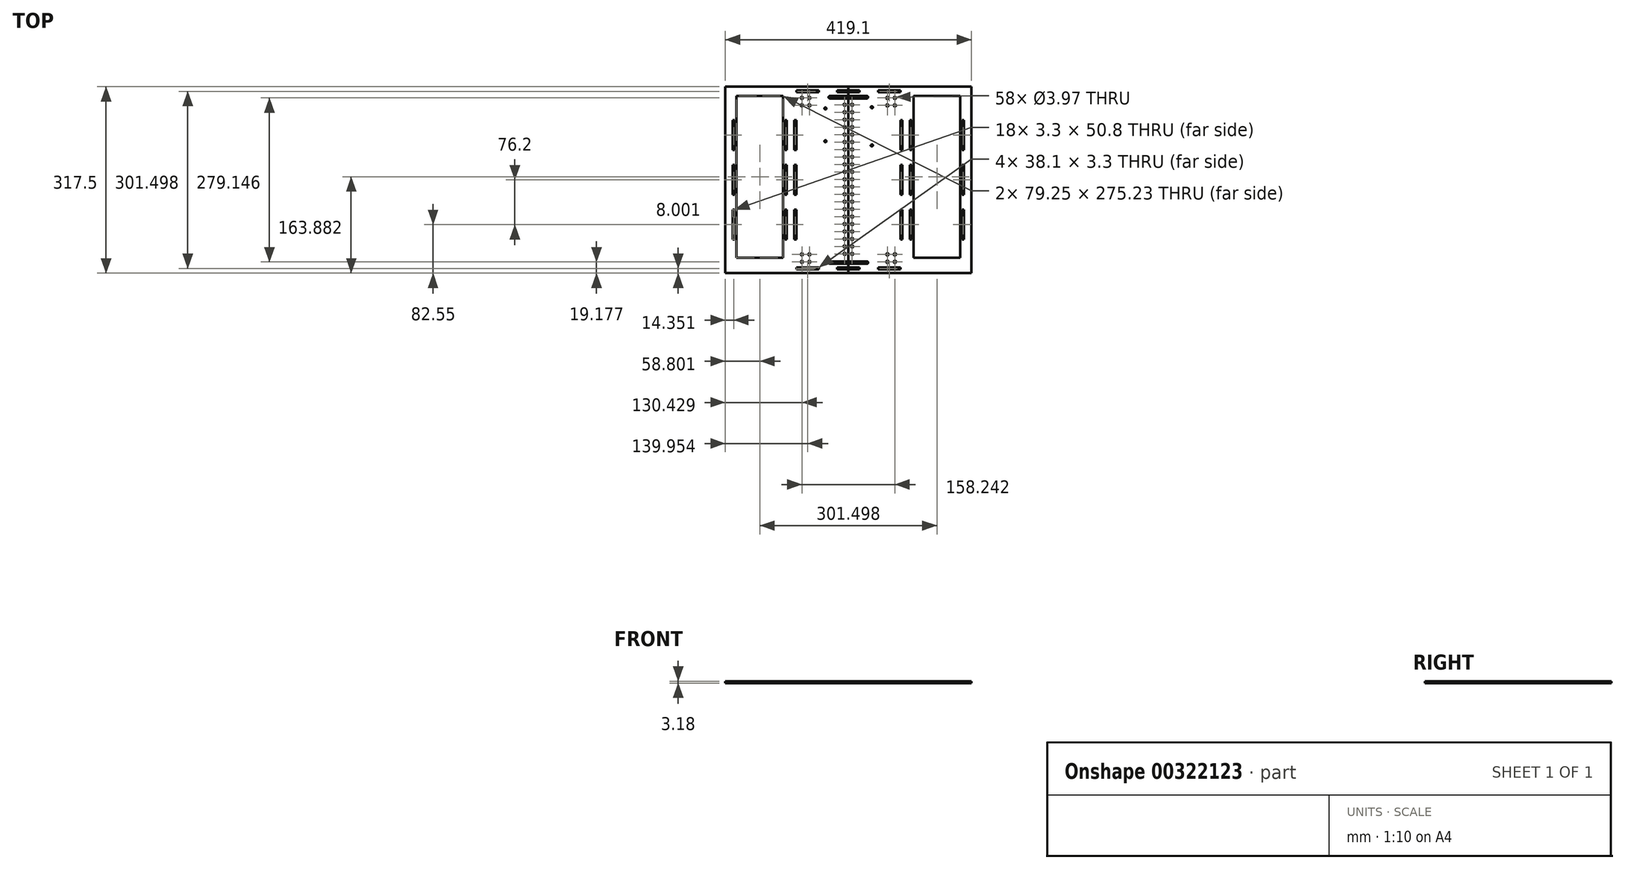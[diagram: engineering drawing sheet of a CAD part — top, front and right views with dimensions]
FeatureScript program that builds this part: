
annotation { "Feature Type Name" : "Feature", "Feature Type Description" : "" }
export const myFeature = defineFeature(function(context is Context, id is Id, definition is map)
    precondition{}
    {
        {
            var Q0;
            Q0=qCreatedBy(makeId("Top.planeOp"),FACE);
            var sketch = newSketch(context, id + "F0", { "sketchPlane" : qUnion([Q0])});
            skLineSegment(sketch, "E0.bottom", {"start": v(111.12, -158.75) * mm, "end": v(-111.12, -158.75) * mm});
            skLineSegment(sketch, "E0.top", {"start": v(111.12, 158.75) * mm, "end": v(-111.12, 158.75) * mm});
            skLineSegment(sketch, "E0.left", {"start": v(111.12, -158.75) * mm, "end": v(111.12, 158.75) * mm, "construction": true});
            skPoint(sketch, "E0.middle", {"position": v(0, 0) * mm});
            skLineSegment(sketch, "E1.bottom", {"start": v(-88.65, 152.4) * mm, "end": v(-50.55, 152.4) * mm});
            skLineSegment(sketch, "E1.top", {"start": v(-88.65, 149.1) * mm, "end": v(-50.55, 149.1) * mm});
            skLineSegment(sketch, "E1.left", {"start": v(-88.65, 152.4) * mm, "end": v(-88.65, 149.1) * mm});
            skLineSegment(sketch, "E1.right", {"start": v(-50.55, 152.4) * mm, "end": v(-50.55, 149.1) * mm});
            skLineSegment(sketch, "E2.bottom", {"start": v(-19.05, 152.4) * mm, "end": v(19.05, 152.4) * mm});
            skLineSegment(sketch, "E2.top", {"start": v(-19.05, 149.1) * mm, "end": v(19.05, 149.1) * mm});
            skLineSegment(sketch, "E2.left", {"start": v(-19.05, 152.4) * mm, "end": v(-19.05, 149.1) * mm});
            skLineSegment(sketch, "E2.right", {"start": v(19.05, 152.4) * mm, "end": v(19.05, 149.1) * mm});
            skLineSegment(sketch, "E3", {"start": v(-50.55, 152.4) * mm, "end": v(-19.05, 152.4) * mm, "construction": true});
            skLineSegment(sketch, "E4.MirrorCS", {"start": v(88.65, 149.1) * mm, "end": v(50.55, 149.1) * mm});
            skLineSegment(sketch, "E5.MirrorCS", {"start": v(88.65, 152.4) * mm, "end": v(50.55, 152.4) * mm});
            skLineSegment(sketch, "E6.MirrorCS", {"start": v(50.55, 152.4) * mm, "end": v(50.55, 149.1) * mm});
            skLineSegment(sketch, "E7.MirrorCS", {"start": v(88.65, 152.4) * mm, "end": v(88.65, 149.1) * mm});
            skLineSegment(sketch, "E8.MirrorCS", {"start": v(-50.55, -152.4) * mm, "end": v(-50.55, -149.1) * mm});
            skLineSegment(sketch, "E9.MirrorCS", {"start": v(-19.05, -149.1) * mm, "end": v(19.05, -149.1) * mm});
            skLineSegment(sketch, "E10.MirrorCS", {"start": v(19.05, -152.4) * mm, "end": v(19.05, -149.1) * mm});
            skLineSegment(sketch, "E11.MirrorCS", {"start": v(88.65, -149.1) * mm, "end": v(50.55, -149.1) * mm});
            skLineSegment(sketch, "E12.MirrorCS", {"start": v(50.55, -152.4) * mm, "end": v(50.55, -149.1) * mm});
            skLineSegment(sketch, "E13.MirrorCS", {"start": v(-88.65, -149.1) * mm, "end": v(-50.55, -149.1) * mm});
            skLineSegment(sketch, "E14.MirrorCS", {"start": v(88.65, -152.4) * mm, "end": v(88.65, -149.1) * mm});
            skLineSegment(sketch, "E15.MirrorCS", {"start": v(-19.05, -152.4) * mm, "end": v(-19.05, -149.1) * mm});
            skLineSegment(sketch, "E16.MirrorCS", {"start": v(88.65, -152.4) * mm, "end": v(50.55, -152.4) * mm});
            skLineSegment(sketch, "E17.MirrorCS", {"start": v(-19.05, -152.4) * mm, "end": v(19.05, -152.4) * mm});
            skLineSegment(sketch, "E18.MirrorCS", {"start": v(-50.55, -152.4) * mm, "end": v(-19.05, -152.4) * mm, "construction": true});
            skLineSegment(sketch, "E19.MirrorCS", {"start": v(-88.65, -152.4) * mm, "end": v(-50.55, -152.4) * mm});
            skLineSegment(sketch, "E20.MirrorCS", {"start": v(-88.65, -152.4) * mm, "end": v(-88.65, -149.1) * mm});
            skLineSegment(sketch, "E21.bottom", {"start": v(-107.95, 101.6) * mm, "end": v(-104.65, 101.6) * mm});
            skLineSegment(sketch, "E21.top", {"start": v(-107.95, 50.8) * mm, "end": v(-104.65, 50.8) * mm});
            skLineSegment(sketch, "E21.left", {"start": v(-107.95, 101.6) * mm, "end": v(-107.95, 50.8) * mm});
            skLineSegment(sketch, "E21.right", {"start": v(-104.65, 101.6) * mm, "end": v(-104.65, 50.8) * mm});
            skLineSegment(sketch, "E22.0.1.0", {"start": v(-104.65, 25.4) * mm, "end": v(-104.65, -25.4) * mm});
            skLineSegment(sketch, "E22.0.1.1", {"start": v(-107.95, 25.4) * mm, "end": v(-107.95, -25.4) * mm});
            skLineSegment(sketch, "E22.0.1.2", {"start": v(-107.95, 25.4) * mm, "end": v(-104.65, 25.4) * mm});
            skLineSegment(sketch, "E22.0.1.3", {"start": v(-107.95, -25.4) * mm, "end": v(-104.65, -25.4) * mm});
            skLineSegment(sketch, "E22.0.2.0", {"start": v(-104.65, -50.8) * mm, "end": v(-104.65, -101.6) * mm});
            skLineSegment(sketch, "E22.0.2.1", {"start": v(-107.95, -50.8) * mm, "end": v(-107.95, -101.6) * mm});
            skLineSegment(sketch, "E22.0.2.2", {"start": v(-107.95, -50.8) * mm, "end": v(-104.65, -50.8) * mm});
            skLineSegment(sketch, "E22.0.2.3", {"start": v(-107.95, -101.6) * mm, "end": v(-104.65, -101.6) * mm});
            skLineSegment(sketch, "E22.direction1", {"start": v(-107.95, 50.8) * mm, "end": v(-91.95, 50.8) * mm, "construction": true});
            skLineSegment(sketch, "E22.direction2", {"start": v(-107.95, 50.8) * mm, "end": v(-107.95, -25.4) * mm, "construction": true});
            skLineSegment(sketch, "E23.MirrorCS", {"start": v(104.65, 25.4) * mm, "end": v(104.65, -25.4) * mm});
            skLineSegment(sketch, "E24.MirrorCS", {"start": v(107.95, -50.8) * mm, "end": v(104.65, -50.8) * mm});
            skLineSegment(sketch, "E25.MirrorCS", {"start": v(107.95, 25.4) * mm, "end": v(107.95, -25.4) * mm});
            skLineSegment(sketch, "E26.MirrorCS", {"start": v(107.95, -101.6) * mm, "end": v(104.65, -101.6) * mm});
            skLineSegment(sketch, "E27.MirrorCS", {"start": v(107.95, 25.4) * mm, "end": v(104.65, 25.4) * mm});
            skLineSegment(sketch, "E28.MirrorCS", {"start": v(107.95, -25.4) * mm, "end": v(104.65, -25.4) * mm});
            skLineSegment(sketch, "E29.MirrorCS", {"start": v(107.95, 50.8) * mm, "end": v(107.95, -25.4) * mm, "construction": true});
            skLineSegment(sketch, "E30.MirrorCS", {"start": v(107.95, 101.6) * mm, "end": v(104.65, 101.6) * mm});
            skLineSegment(sketch, "E31.MirrorCS", {"start": v(107.95, 50.8) * mm, "end": v(104.65, 50.8) * mm});
            skLineSegment(sketch, "E32.MirrorCS", {"start": v(107.95, 101.6) * mm, "end": v(107.95, 50.8) * mm});
            skLineSegment(sketch, "E33.MirrorCS", {"start": v(104.65, -50.8) * mm, "end": v(104.65, -101.6) * mm});
            skLineSegment(sketch, "E34.MirrorCS", {"start": v(104.65, 101.6) * mm, "end": v(104.65, 50.8) * mm});
            skLineSegment(sketch, "E35.MirrorCS", {"start": v(107.95, -50.8) * mm, "end": v(107.95, -101.6) * mm});
            skPoint(sketch, "E36.middle", {"position": v(0, 93.75) * mm});
            skCircle(sketch, "E37", {"center": v(39.92, 123.7) * mm, "radius": 1.75 * mm});
            skCircle(sketch, "E38", {"center": v(39.92, 58.7) * mm, "radius": 1.75 * mm});
            skCircle(sketch, "E39", {"center": v(-39.04, 65.88) * mm, "radius": 1.75 * mm});
            skCircle(sketch, "E40.MirrorC", {"center": v(-39.04, 121.62) * mm, "radius": 1.75 * mm});
            skLineSegment(sketch, "E41.0.1.0", {"start": v(-88.65, 101.6) * mm, "end": v(-88.65, 50.8) * mm});
            skLineSegment(sketch, "E41.3.1.0", {"start": v(-91.95, 101.6) * mm, "end": v(-91.95, 50.8) * mm});
            skLineSegment(sketch, "E41.6.1.0", {"start": v(-91.95, 101.6) * mm, "end": v(-88.65, 101.6) * mm});
            skLineSegment(sketch, "E41.9.1.0", {"start": v(-91.95, 50.8) * mm, "end": v(-88.65, 50.8) * mm});
            skLineSegment(sketch, "E41.0.1.1", {"start": v(-88.65, 25.4) * mm, "end": v(-88.65, -25.4) * mm});
            skLineSegment(sketch, "E41.3.1.1", {"start": v(-91.95, 25.4) * mm, "end": v(-91.95, -25.4) * mm});
            skLineSegment(sketch, "E41.6.1.1", {"start": v(-91.95, 25.4) * mm, "end": v(-88.65, 25.4) * mm});
            skLineSegment(sketch, "E41.9.1.1", {"start": v(-91.95, -25.4) * mm, "end": v(-88.65, -25.4) * mm});
            skLineSegment(sketch, "E41.0.1.2", {"start": v(-88.65, -50.8) * mm, "end": v(-88.65, -101.6) * mm});
            skLineSegment(sketch, "E41.3.1.2", {"start": v(-91.95, -50.8) * mm, "end": v(-91.95, -101.6) * mm});
            skLineSegment(sketch, "E41.6.1.2", {"start": v(-91.95, -50.8) * mm, "end": v(-88.65, -50.8) * mm});
            skLineSegment(sketch, "E41.9.1.2", {"start": v(-91.95, -101.6) * mm, "end": v(-88.65, -101.6) * mm});
            skLineSegment(sketch, "E42.MirrorCS", {"start": v(91.95, 101.6) * mm, "end": v(91.95, 50.8) * mm});
            skLineSegment(sketch, "E43.MirrorCS", {"start": v(91.95, 101.6) * mm, "end": v(88.65, 101.6) * mm});
            skLineSegment(sketch, "E44.MirrorCS", {"start": v(91.95, 50.8) * mm, "end": v(88.65, 50.8) * mm});
            skLineSegment(sketch, "E45.MirrorCS", {"start": v(91.95, -50.8) * mm, "end": v(91.95, -101.6) * mm});
            skLineSegment(sketch, "E46.MirrorCS", {"start": v(88.65, 25.4) * mm, "end": v(88.65, -25.4) * mm});
            skLineSegment(sketch, "E47.MirrorCS", {"start": v(91.95, -50.8) * mm, "end": v(88.65, -50.8) * mm});
            skLineSegment(sketch, "E48.MirrorCS", {"start": v(91.95, 25.4) * mm, "end": v(91.95, -25.4) * mm});
            skLineSegment(sketch, "E49.MirrorCS", {"start": v(91.95, -101.6) * mm, "end": v(88.65, -101.6) * mm});
            skLineSegment(sketch, "E50.MirrorCS", {"start": v(91.95, 25.4) * mm, "end": v(88.65, 25.4) * mm});
            skLineSegment(sketch, "E51.MirrorCS", {"start": v(91.95, -25.4) * mm, "end": v(88.65, -25.4) * mm});
            skLineSegment(sketch, "E52.MirrorCS", {"start": v(88.65, 101.6) * mm, "end": v(88.65, 50.8) * mm});
            skLineSegment(sketch, "E53.MirrorCS", {"start": v(88.65, -50.8) * mm, "end": v(88.65, -101.6) * mm});
            skLineSegment(sketch, "E54", {"start": v(-88.65, 101.6) * mm, "end": v(-88.65, 149.1) * mm, "construction": true});
            skCircle(sketch, "E55", {"center": v(-79.12, 139.57) * mm, "radius": 1.98 * mm});
            skCircle(sketch, "E56", {"center": v(-66.42, 139.57) * mm, "radius": 1.98 * mm});
            skCircle(sketch, "E57", {"center": v(-79.12, 126.87) * mm, "radius": 1.98 * mm});
            skCircle(sketch, "E58", {"center": v(-66.42, 126.87) * mm, "radius": 1.98 * mm});
            skCircle(sketch, "E59.MirrorC", {"center": v(79.12, 126.87) * mm, "radius": 1.98 * mm});
            skCircle(sketch, "E60.MirrorC", {"center": v(79.12, 139.57) * mm, "radius": 1.98 * mm});
            skCircle(sketch, "E61.MirrorC", {"center": v(66.42, 139.57) * mm, "radius": 1.98 * mm});
            skCircle(sketch, "E62.MirrorC", {"center": v(66.42, 126.87) * mm, "radius": 1.98 * mm});
            skCircle(sketch, "E63.MirrorC", {"center": v(-79.12, -139.57) * mm, "radius": 1.98 * mm});
            skCircle(sketch, "E64.MirrorC", {"center": v(-79.12, -126.87) * mm, "radius": 1.98 * mm});
            skCircle(sketch, "E65.MirrorC", {"center": v(-66.42, -139.57) * mm, "radius": 1.98 * mm});
            skCircle(sketch, "E66.MirrorC", {"center": v(-66.42, -126.87) * mm, "radius": 1.98 * mm});
            skCircle(sketch, "E67.MirrorC", {"center": v(66.42, -139.57) * mm, "radius": 1.98 * mm});
            skCircle(sketch, "E68.MirrorC", {"center": v(79.12, -126.87) * mm, "radius": 1.98 * mm});
            skCircle(sketch, "E69.MirrorC", {"center": v(66.42, -126.87) * mm, "radius": 1.98 * mm});
            skCircle(sketch, "E70.MirrorC", {"center": v(79.12, -139.57) * mm, "radius": 1.98 * mm});
            skLineSegment(sketch, "E71.bottom", {"start": v(228.6, -228.6) * mm, "end": v(-228.6, -228.6) * mm, "construction": true});
            skLineSegment(sketch, "E71.top", {"start": v(228.6, 228.6) * mm, "end": v(-228.6, 228.6) * mm, "construction": true});
            skLineSegment(sketch, "E71.left", {"start": v(228.6, -228.6) * mm, "end": v(228.6, 228.6) * mm, "construction": true});
            skLineSegment(sketch, "E71.right", {"start": v(-228.6, -228.6) * mm, "end": v(-228.6, 228.6) * mm, "construction": true});
            skLineSegment(sketch, "E72", {"start": v(111.12, 158.75) * mm, "end": v(209.55, 158.75) * mm});
            skLineSegment(sketch, "E73", {"start": v(209.55, 158.75) * mm, "end": v(209.55, -158.75) * mm});
            skLineSegment(sketch, "E74", {"start": v(209.55, -158.75) * mm, "end": v(111.12, -158.75) * mm});
            skLineSegment(sketch, "E75.bottom", {"start": v(111.12, 142.75) * mm, "end": v(190.37, 142.75) * mm});
            skLineSegment(sketch, "E75.top", {"start": v(111.12, -132.48) * mm, "end": v(190.37, -132.48) * mm});
            skLineSegment(sketch, "E75.left", {"start": v(111.12, 142.75) * mm, "end": v(111.12, -132.48) * mm});
            skLineSegment(sketch, "E75.right", {"start": v(190.37, 142.75) * mm, "end": v(190.37, -132.48) * mm});
            skLineSegment(sketch, "E76.1.0.0", {"start": v(196.85, -25.4) * mm, "end": v(193.55, -25.4) * mm});
            skLineSegment(sketch, "E76.1.0.1", {"start": v(193.55, -50.8) * mm, "end": v(193.55, -101.6) * mm});
            skLineSegment(sketch, "E76.1.0.2", {"start": v(196.85, 101.6) * mm, "end": v(196.85, 50.8) * mm});
            skLineSegment(sketch, "E76.1.0.3", {"start": v(196.85, 50.8) * mm, "end": v(193.55, 50.8) * mm});
            skLineSegment(sketch, "E76.1.0.4", {"start": v(196.85, 25.4) * mm, "end": v(193.55, 25.4) * mm});
            skLineSegment(sketch, "E76.1.0.5", {"start": v(196.85, 50.8) * mm, "end": v(196.85, -25.4) * mm, "construction": true});
            skLineSegment(sketch, "E76.1.0.6", {"start": v(193.55, 25.4) * mm, "end": v(193.55, -25.4) * mm});
            skLineSegment(sketch, "E76.1.0.7", {"start": v(193.55, 101.6) * mm, "end": v(193.55, 50.8) * mm});
            skLineSegment(sketch, "E76.1.0.8", {"start": v(196.85, 25.4) * mm, "end": v(196.85, -25.4) * mm});
            skLineSegment(sketch, "E76.1.0.9", {"start": v(196.85, -50.8) * mm, "end": v(193.55, -50.8) * mm});
            skLineSegment(sketch, "E76.1.0.10", {"start": v(196.85, -101.6) * mm, "end": v(193.55, -101.6) * mm});
            skLineSegment(sketch, "E76.1.0.11", {"start": v(196.85, -50.8) * mm, "end": v(196.85, -101.6) * mm});
            skLineSegment(sketch, "E76.1.0.12", {"start": v(196.85, 101.6) * mm, "end": v(193.55, 101.6) * mm});
            skLineSegment(sketch, "E76.direction1", {"start": v(104.65, -101.6) * mm, "end": v(193.55, -101.6) * mm, "construction": true});
            skLineSegment(sketch, "E77.MirrorCS", {"start": v(-196.85, 50.8) * mm, "end": v(-196.85, -25.4) * mm, "construction": true});
            skLineSegment(sketch, "E78.MirrorCS", {"start": v(-196.85, -101.6) * mm, "end": v(-193.55, -101.6) * mm});
            skLineSegment(sketch, "E79.MirrorCS", {"start": v(-111.12, -158.75) * mm, "end": v(-111.12, 158.75) * mm, "construction": true});
            skLineSegment(sketch, "E80.MirrorCS", {"start": v(-196.85, 101.6) * mm, "end": v(-193.55, 101.6) * mm});
            skLineSegment(sketch, "E81.MirrorCS", {"start": v(-193.55, -50.8) * mm, "end": v(-193.55, -101.6) * mm});
            skLineSegment(sketch, "E82.MirrorCS", {"start": v(-193.55, 101.6) * mm, "end": v(-193.55, 50.8) * mm});
            skLineSegment(sketch, "E83.MirrorCS", {"start": v(-111.12, 158.75) * mm, "end": v(-209.55, 158.75) * mm});
            skLineSegment(sketch, "E84.MirrorCS", {"start": v(-196.85, 50.8) * mm, "end": v(-193.55, 50.8) * mm});
            skLineSegment(sketch, "E85.MirrorCS", {"start": v(-209.55, -158.75) * mm, "end": v(-111.12, -158.75) * mm});
            skLineSegment(sketch, "E86.MirrorCS", {"start": v(-196.85, -50.8) * mm, "end": v(-193.55, -50.8) * mm});
            skLineSegment(sketch, "E87.MirrorCS", {"start": v(-196.85, -50.8) * mm, "end": v(-196.85, -101.6) * mm});
            skLineSegment(sketch, "E88.MirrorCS", {"start": v(-196.85, -25.4) * mm, "end": v(-193.55, -25.4) * mm});
            skLineSegment(sketch, "E89.MirrorCS", {"start": v(-111.12, -132.48) * mm, "end": v(-190.37, -132.48) * mm});
            skLineSegment(sketch, "E90.MirrorCS", {"start": v(-193.55, 25.4) * mm, "end": v(-193.55, -25.4) * mm});
            skLineSegment(sketch, "E91.MirrorCS", {"start": v(-196.85, 101.6) * mm, "end": v(-196.85, 50.8) * mm});
            skLineSegment(sketch, "E92.MirrorCS", {"start": v(-196.85, 25.4) * mm, "end": v(-196.85, -25.4) * mm});
            skLineSegment(sketch, "E93.MirrorCS", {"start": v(-209.55, 158.75) * mm, "end": v(-209.55, -158.75) * mm});
            skLineSegment(sketch, "E94.MirrorCS", {"start": v(-190.37, 142.75) * mm, "end": v(-190.37, -132.48) * mm});
            skLineSegment(sketch, "E95.MirrorCS", {"start": v(-196.85, 25.4) * mm, "end": v(-193.55, 25.4) * mm});
            skLineSegment(sketch, "E96.MirrorCS", {"start": v(-111.12, 142.75) * mm, "end": v(-190.37, 142.75) * mm});
            skLineSegment(sketch, "E97", {"start": v(-111.12, 142.75) * mm, "end": v(-111.12, -132.48) * mm});
            skPoint(sketch, "E98", {"position": v(0, 149.1) * mm});
            skLineSegment(sketch, "E99", {"start": v(0, 142.75) * mm, "end": v(-31.75, 142.75) * mm});
            skArc(sketch, "E100", {"start": v(-31.75, 142.75) * mm, "mid": v(-33.73, 140.76) * mm, "end": v(-31.75, 138.78) * mm});
            skLineSegment(sketch, "E101", {"start": v(-31.75, 138.78) * mm, "end": v(0, 138.78) * mm});
            skLineSegment(sketch, "E102.MirrorCS", {"start": v(0, 142.75) * mm, "end": v(31.75, 142.75) * mm});
            skArc(sketch, "E103.MirrorCS", {"start": v(31.75, 142.75) * mm, "mid": v(33.73, 140.76) * mm, "end": v(31.75, 138.78) * mm});
            skLineSegment(sketch, "E104.MirrorCS", {"start": v(31.75, 138.78) * mm, "end": v(0, 138.78) * mm});
            skLineSegment(sketch, "E105.MirrorCS", {"start": v(-31.75, -138.78) * mm, "end": v(0, -138.78) * mm});
            skLineSegment(sketch, "E106.MirrorCS", {"start": v(31.75, -138.78) * mm, "end": v(0, -138.78) * mm});
            skLineSegment(sketch, "E107.MirrorCS", {"start": v(0, -142.75) * mm, "end": v(31.75, -142.75) * mm});
            skLineSegment(sketch, "E108.MirrorCS", {"start": v(0, -142.75) * mm, "end": v(-31.75, -142.75) * mm});
            skArc(sketch, "E109.MirrorCS", {"start": v(-31.75, -142.75) * mm, "mid": v(-33.73, -140.76) * mm, "end": v(-31.75, -138.78) * mm});
            skArc(sketch, "E110.MirrorCS", {"start": v(31.75, -142.75) * mm, "mid": v(33.73, -140.76) * mm, "end": v(31.75, -138.78) * mm});
            skLineSegment(sketch, "E111", {"start": v(0, 158.75) * mm, "end": v(0, -158.75) * mm});
            skCircle(sketch, "E112", {"center": v(-6.35, -126.08) * mm, "radius": 1.98 * mm});
            skCircle(sketch, "E113.0.1.0", {"center": v(-6.35, -113.38) * mm, "radius": 1.98 * mm});
            skCircle(sketch, "E113.0.2.0", {"center": v(-6.35, -100.68) * mm, "radius": 1.98 * mm});
            skCircle(sketch, "E113.0.3.0", {"center": v(-6.35, -87.98) * mm, "radius": 1.98 * mm});
            skCircle(sketch, "E113.0.4.0", {"center": v(-6.35, -75.28) * mm, "radius": 1.98 * mm});
            skCircle(sketch, "E113.0.5.0", {"center": v(-6.35, -62.58) * mm, "radius": 1.98 * mm});
            skCircle(sketch, "E113.0.6.0", {"center": v(-6.35, -49.88) * mm, "radius": 1.98 * mm});
            skCircle(sketch, "E113.0.7.0", {"center": v(-6.35, -37.18) * mm, "radius": 1.98 * mm});
            skCircle(sketch, "E113.0.8.0", {"center": v(-6.35, -24.48) * mm, "radius": 1.98 * mm});
            skCircle(sketch, "E113.0.9.0", {"center": v(-6.35, -11.78) * mm, "radius": 1.98 * mm});
            skCircle(sketch, "E113.0.10.0", {"center": v(-6.35, 0.92) * mm, "radius": 1.98 * mm});
            skCircle(sketch, "E113.0.11.0", {"center": v(-6.35, 13.62) * mm, "radius": 1.98 * mm});
            skCircle(sketch, "E113.0.12.0", {"center": v(-6.35, 26.32) * mm, "radius": 1.98 * mm});
            skCircle(sketch, "E113.0.13.0", {"center": v(-6.35, 39.02) * mm, "radius": 1.98 * mm});
            skCircle(sketch, "E113.0.14.0", {"center": v(-6.35, 51.72) * mm, "radius": 1.98 * mm});
            skCircle(sketch, "E113.0.15.0", {"center": v(-6.35, 64.42) * mm, "radius": 1.98 * mm});
            skCircle(sketch, "E113.0.16.0", {"center": v(-6.35, 77.12) * mm, "radius": 1.98 * mm});
            skCircle(sketch, "E113.0.17.0", {"center": v(-6.35, 89.82) * mm, "radius": 1.98 * mm});
            skCircle(sketch, "E113.0.18.0", {"center": v(-6.35, 102.52) * mm, "radius": 1.98 * mm});
            skCircle(sketch, "E113.0.19.0", {"center": v(-6.35, 115.22) * mm, "radius": 1.98 * mm});
            skCircle(sketch, "E113.0.20.0", {"center": v(-6.35, 127.92) * mm, "radius": 1.98 * mm});
            skCircle(sketch, "E113.1.0.0", {"center": v(6.35, -126.08) * mm, "radius": 1.98 * mm});
            skCircle(sketch, "E113.1.1.0", {"center": v(6.35, -113.38) * mm, "radius": 1.98 * mm});
            skCircle(sketch, "E113.1.2.0", {"center": v(6.35, -100.68) * mm, "radius": 1.98 * mm});
            skCircle(sketch, "E113.1.3.0", {"center": v(6.35, -87.98) * mm, "radius": 1.98 * mm});
            skCircle(sketch, "E113.1.4.0", {"center": v(6.35, -75.28) * mm, "radius": 1.98 * mm});
            skCircle(sketch, "E113.1.5.0", {"center": v(6.35, -62.58) * mm, "radius": 1.98 * mm});
            skCircle(sketch, "E113.1.6.0", {"center": v(6.35, -49.88) * mm, "radius": 1.98 * mm});
            skCircle(sketch, "E113.1.7.0", {"center": v(6.35, -37.18) * mm, "radius": 1.98 * mm});
            skCircle(sketch, "E113.1.8.0", {"center": v(6.35, -24.48) * mm, "radius": 1.98 * mm});
            skCircle(sketch, "E113.1.9.0", {"center": v(6.35, -11.78) * mm, "radius": 1.98 * mm});
            skCircle(sketch, "E113.1.10.0", {"center": v(6.35, 0.92) * mm, "radius": 1.98 * mm});
            skCircle(sketch, "E113.1.11.0", {"center": v(6.35, 13.62) * mm, "radius": 1.98 * mm});
            skCircle(sketch, "E113.1.12.0", {"center": v(6.35, 26.32) * mm, "radius": 1.98 * mm});
            skCircle(sketch, "E113.1.13.0", {"center": v(6.35, 39.02) * mm, "radius": 1.98 * mm});
            skCircle(sketch, "E113.1.14.0", {"center": v(6.35, 51.72) * mm, "radius": 1.98 * mm});
            skCircle(sketch, "E113.1.15.0", {"center": v(6.35, 64.42) * mm, "radius": 1.98 * mm});
            skCircle(sketch, "E113.1.16.0", {"center": v(6.35, 77.12) * mm, "radius": 1.98 * mm});
            skCircle(sketch, "E113.1.17.0", {"center": v(6.35, 89.82) * mm, "radius": 1.98 * mm});
            skCircle(sketch, "E113.1.18.0", {"center": v(6.35, 102.52) * mm, "radius": 1.98 * mm});
            skCircle(sketch, "E113.1.19.0", {"center": v(6.35, 115.22) * mm, "radius": 1.98 * mm});
            skCircle(sketch, "E113.1.20.0", {"center": v(6.35, 127.92) * mm, "radius": 1.98 * mm});
            skLineSegment(sketch, "E113.direction1", {"start": v(-6.35, -126.08) * mm, "end": v(6.35, -126.08) * mm, "construction": true});
            skLineSegment(sketch, "E113.direction2", {"start": v(-6.35, -126.08) * mm, "end": v(-6.35, -113.38) * mm, "construction": true});
            skSolve(sketch);
        }
        {
            var Q0;
            Q0=makeQuery(id+"F0.imprint","IMPRINT",FACE,{"disambiguationData":[TD([[makeQuery(id+"F0.imprint","IMPRINT",EDGE,{"derivedFrom":sQuery(id+"F0.wireOp",EDGE,"E1.bottom")}),1.0]])]});
            extrude(context, id + "F1", {"entities" : qUnion([Q0]), "depth" : 3.17 * mm});
        }
        {
            var Q0;
            {var subQ14=sQuery(id+"F0.wireOp",EDGE,"E2.right");Q0=makeQuery(id+"F0.imprint","IMPRINT",FACE,{"disambiguationData":[TD([[makeQuery(id+"F0.imprint","IMPRINT",EDGE,{"derivedFrom":subQ14}),1.0]])]});}
            extrude(context, id + "F2", {"entities" : qUnion([Q0]), "depth" : 3.17 * mm});
        }
    });
